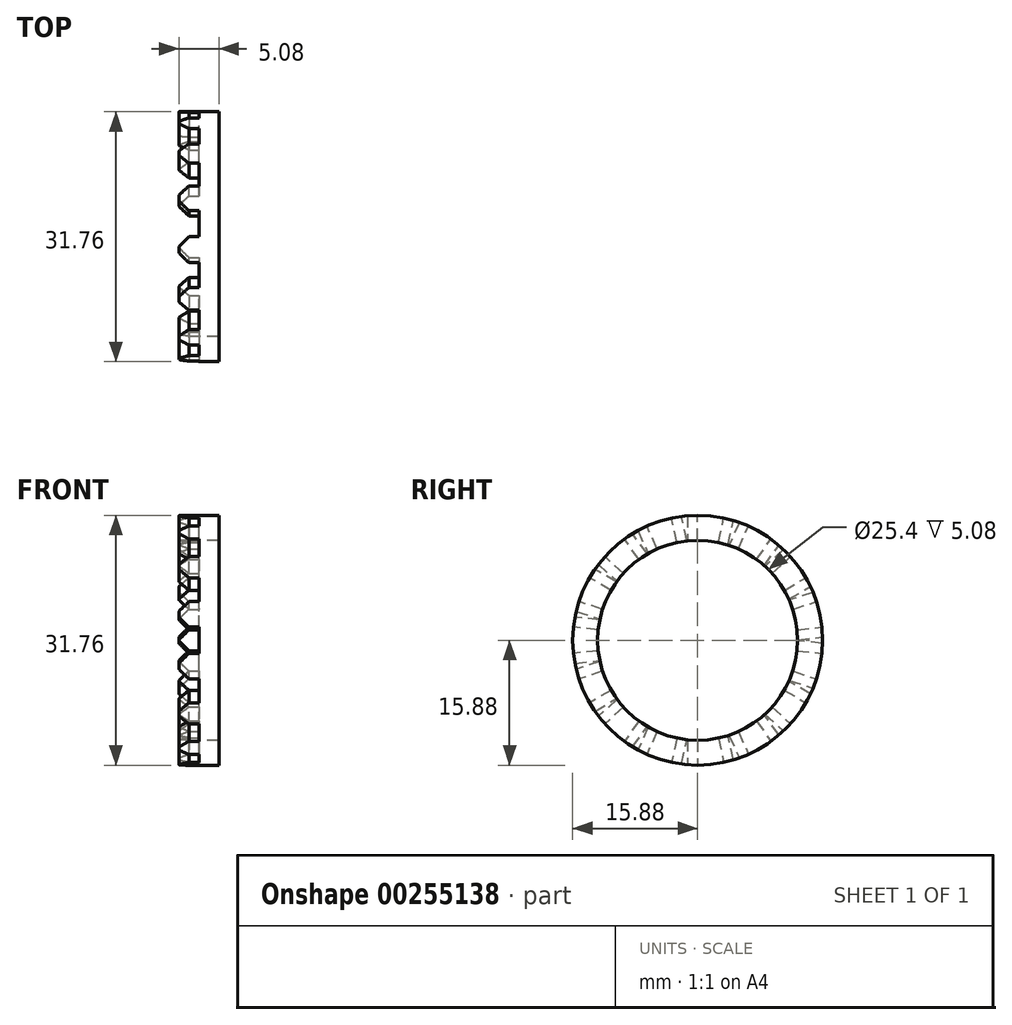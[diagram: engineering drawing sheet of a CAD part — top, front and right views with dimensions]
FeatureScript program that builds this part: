
annotation { "Feature Type Name" : "Feature", "Feature Type Description" : "" }
export const myFeature = defineFeature(function(context is Context, id is Id, definition is map)
    precondition{}
    {
        {
            var Q0;
            Q0=qCreatedBy(makeId("Right.planeOp"),FACE);
            var sketch = newSketch(context, id + "F0", { "sketchPlane" : qUnion([Q0])});
            skCircle(sketch, "E0", {"center": v(0, 0) * mm, "radius": 12.7 * mm});
            skCircle(sketch, "E1", {"center": v(0, 0) * mm, "radius": 15.88 * mm});
            skSolve(sketch);
        }
        {
            var Q0;
            Q0 = qSketchRegion(id + "F0", true);
            extrude(context, id + "F1", {"entities" : qUnion([Q0]), "depth" : 5.08 * mm});
        }
        {
            var Q0;
            Q0=makeQuery(id+"F1.opExtrude","CAP_FACE",FACE,{"disambiguationData":[OSD([sQuery(id+"F0.wireOp",EDGE,"E0"),sQuery(id+"F0.wireOp",EDGE,"E1")])],"isStart":true});
            var sketch = newSketch(context, id + "F2", { "sketchPlane" : qUnion([Q0])});
            skLineSegment(sketch, "E2", {"start": v(0, 12.7) * mm, "end": v(0, 15.88) * mm});
            skLineSegment(sketch, "E3.1.0", {"start": v(-2.64, 12.42) * mm, "end": v(-3.3, 15.53) * mm});
            skLineSegment(sketch, "E3.2.0", {"start": v(-5.17, 11.6) * mm, "end": v(-6.46, 14.5) * mm});
            skLineSegment(sketch, "E3.3.0", {"start": v(-7.46, 10.27) * mm, "end": v(-9.33, 12.84) * mm});
            skLineSegment(sketch, "E3.4.0", {"start": v(-9.44, 8.5) * mm, "end": v(-11.8, 10.62) * mm});
            skLineSegment(sketch, "E3.5.0", {"start": v(-11, 6.35) * mm, "end": v(-13.75, 7.94) * mm});
            skLineSegment(sketch, "E3.6.0", {"start": v(-12.08, 3.92) * mm, "end": v(-15.1, 4.9) * mm});
            skLineSegment(sketch, "E3.7.0", {"start": v(-12.63, 1.33) * mm, "end": v(-15.79, 1.66) * mm});
            skLineSegment(sketch, "E3.8.0", {"start": v(-12.63, -1.33) * mm, "end": v(-15.79, -1.66) * mm});
            skLineSegment(sketch, "E3.9.0", {"start": v(-12.08, -3.92) * mm, "end": v(-15.1, -4.9) * mm});
            skLineSegment(sketch, "E3.10.0", {"start": v(-11, -6.35) * mm, "end": v(-13.75, -7.94) * mm});
            skLineSegment(sketch, "E3.11.0", {"start": v(-9.44, -8.5) * mm, "end": v(-11.8, -10.62) * mm});
            skLineSegment(sketch, "E3.12.0", {"start": v(-7.46, -10.27) * mm, "end": v(-9.33, -12.84) * mm});
            skLineSegment(sketch, "E3.13.0", {"start": v(-5.17, -11.6) * mm, "end": v(-6.46, -14.5) * mm});
            skLineSegment(sketch, "E3.14.0", {"start": v(-2.64, -12.42) * mm, "end": v(-3.3, -15.53) * mm});
            skLineSegment(sketch, "E3.15.0", {"start": v(0, -12.7) * mm, "end": v(0, -15.88) * mm});
            skLineSegment(sketch, "E3.16.0", {"start": v(2.64, -12.42) * mm, "end": v(3.3, -15.53) * mm});
            skLineSegment(sketch, "E3.17.0", {"start": v(5.17, -11.6) * mm, "end": v(6.46, -14.5) * mm});
            skLineSegment(sketch, "E3.18.0", {"start": v(7.46, -10.27) * mm, "end": v(9.33, -12.84) * mm});
            skLineSegment(sketch, "E3.19.0", {"start": v(9.44, -8.5) * mm, "end": v(11.8, -10.62) * mm});
            skLineSegment(sketch, "E3.20.0", {"start": v(11, -6.35) * mm, "end": v(13.75, -7.94) * mm});
            skLineSegment(sketch, "E3.21.0", {"start": v(12.08, -3.92) * mm, "end": v(15.1, -4.9) * mm});
            skLineSegment(sketch, "E3.22.0", {"start": v(12.63, -1.33) * mm, "end": v(15.79, -1.66) * mm});
            skLineSegment(sketch, "E3.23.0", {"start": v(12.63, 1.33) * mm, "end": v(15.79, 1.66) * mm});
            skLineSegment(sketch, "E3.24.0", {"start": v(12.08, 3.92) * mm, "end": v(15.1, 4.9) * mm});
            skLineSegment(sketch, "E3.25.0", {"start": v(11, 6.35) * mm, "end": v(13.75, 7.94) * mm});
            skLineSegment(sketch, "E3.26.0", {"start": v(9.44, 8.5) * mm, "end": v(11.8, 10.62) * mm});
            skLineSegment(sketch, "E3.27.0", {"start": v(7.46, 10.27) * mm, "end": v(9.33, 12.84) * mm});
            skLineSegment(sketch, "E3.28.0", {"start": v(5.17, 11.6) * mm, "end": v(6.46, 14.5) * mm});
            skLineSegment(sketch, "E3.29.0", {"start": v(2.64, 12.42) * mm, "end": v(3.3, 15.53) * mm});
            skPoint(sketch, "E3.center", {"position": v(0, 0) * mm});
            skCircle(sketch, "E4", {"center": v(0, 0) * mm, "radius": 15.88 * mm});
            skCircle(sketch, "E5", {"center": v(0, 0) * mm, "radius": 12.7 * mm});
            skSolve(sketch);
        }
        {
            var Q0;
            {var subQ0=sQuery(id+"F2.wireOp",EDGE,"E3.1.0");Q0=makeQuery(id+"F2.imprint","IMPRINT",FACE,{"disambiguationData":[TD([[makeQuery(id+"F2.imprint","IMPRINT",EDGE,{"derivedFrom":subQ0}),1.0]])]});}
            var Q1;
            {var subQ0=sQuery(id+"F2.wireOp",EDGE,"E2");Q1=makeQuery(id+"F2.imprint","IMPRINT",FACE,{"disambiguationData":[TD([[makeQuery(id+"F2.imprint","IMPRINT",EDGE,{"derivedFrom":subQ0}),-1.0]])]});}
            var Q2;
            {var subQ0=sQuery(id+"F2.wireOp",EDGE,"E3.27.0");Q2=makeQuery(id+"F2.imprint","IMPRINT",FACE,{"disambiguationData":[TD([[makeQuery(id+"F2.imprint","IMPRINT",EDGE,{"derivedFrom":subQ0}),1.0]])]});}
            var Q3;
            {var subQ0=sQuery(id+"F2.wireOp",EDGE,"E3.25.0");Q3=makeQuery(id+"F2.imprint","IMPRINT",FACE,{"disambiguationData":[TD([[makeQuery(id+"F2.imprint","IMPRINT",EDGE,{"derivedFrom":subQ0}),1.0]])]});}
            var Q4;
            {var subQ0=sQuery(id+"F2.wireOp",EDGE,"E3.23.0");Q4=makeQuery(id+"F2.imprint","IMPRINT",FACE,{"disambiguationData":[TD([[makeQuery(id+"F2.imprint","IMPRINT",EDGE,{"derivedFrom":subQ0}),1.0]])]});}
            var Q5;
            {var subQ0=sQuery(id+"F2.wireOp",EDGE,"E3.21.0");Q5=makeQuery(id+"F2.imprint","IMPRINT",FACE,{"disambiguationData":[TD([[makeQuery(id+"F2.imprint","IMPRINT",EDGE,{"derivedFrom":subQ0}),1.0]])]});}
            var Q6;
            {var subQ0=sQuery(id+"F2.wireOp",EDGE,"E3.19.0");Q6=makeQuery(id+"F2.imprint","IMPRINT",FACE,{"disambiguationData":[TD([[makeQuery(id+"F2.imprint","IMPRINT",EDGE,{"derivedFrom":subQ0}),1.0]])]});}
            var Q7;
            {var subQ0=sQuery(id+"F2.wireOp",EDGE,"E3.17.0");Q7=makeQuery(id+"F2.imprint","IMPRINT",FACE,{"disambiguationData":[TD([[makeQuery(id+"F2.imprint","IMPRINT",EDGE,{"derivedFrom":subQ0}),1.0]])]});}
            var Q8;
            {var subQ0=sQuery(id+"F2.wireOp",EDGE,"E3.15.0");Q8=makeQuery(id+"F2.imprint","IMPRINT",FACE,{"disambiguationData":[TD([[makeQuery(id+"F2.imprint","IMPRINT",EDGE,{"derivedFrom":subQ0}),1.0]])]});}
            var Q9;
            {var subQ0=sQuery(id+"F2.wireOp",EDGE,"E3.13.0");Q9=makeQuery(id+"F2.imprint","IMPRINT",FACE,{"disambiguationData":[TD([[makeQuery(id+"F2.imprint","IMPRINT",EDGE,{"derivedFrom":subQ0}),1.0]])]});}
            var Q10;
            {var subQ0=sQuery(id+"F2.wireOp",EDGE,"E3.11.0");Q10=makeQuery(id+"F2.imprint","IMPRINT",FACE,{"disambiguationData":[TD([[makeQuery(id+"F2.imprint","IMPRINT",EDGE,{"derivedFrom":subQ0}),1.0]])]});}
            var Q11;
            {var subQ0=sQuery(id+"F2.wireOp",EDGE,"E3.9.0");Q11=makeQuery(id+"F2.imprint","IMPRINT",FACE,{"disambiguationData":[TD([[makeQuery(id+"F2.imprint","IMPRINT",EDGE,{"derivedFrom":subQ0}),1.0]])]});}
            var Q12;
            {var subQ0=sQuery(id+"F2.wireOp",EDGE,"E3.7.0");Q12=makeQuery(id+"F2.imprint","IMPRINT",FACE,{"disambiguationData":[TD([[makeQuery(id+"F2.imprint","IMPRINT",EDGE,{"derivedFrom":subQ0}),1.0]])]});}
            var Q13;
            {var subQ0=sQuery(id+"F2.wireOp",EDGE,"E3.5.0");Q13=makeQuery(id+"F2.imprint","IMPRINT",FACE,{"disambiguationData":[TD([[makeQuery(id+"F2.imprint","IMPRINT",EDGE,{"derivedFrom":subQ0}),1.0]])]});}
            var Q14;
            {var subQ0=sQuery(id+"F2.wireOp",EDGE,"E3.3.0");Q14=makeQuery(id+"F2.imprint","IMPRINT",FACE,{"disambiguationData":[TD([[makeQuery(id+"F2.imprint","IMPRINT",EDGE,{"derivedFrom":subQ0}),1.0]])]});}
            extrude(context, id + "F3", {"entities" : qUnion([Q0, Q1, Q2, Q3, Q4, Q5, Q6, Q7, Q8, Q9, Q10, Q11, Q12, Q13, Q14]), "operationType" : NewBodyOperationType.ADD, "depth" : 2.54 * mm});
        }
        {
            var Q0;
            Q0=makeQuery(id+"F3.opExtrude","CAP_EDGE",EDGE,{"disambiguationData":[OSD([sQuery(id+"F2.wireOp",EDGE,"E3.5.0")])],"isStart":false});
            var Q1;
            Q1=makeQuery(id+"F3.opExtrude","CAP_EDGE",EDGE,{"disambiguationData":[OSD([sQuery(id+"F2.wireOp",EDGE,"E3.6.0")])],"isStart":false});
            var Q2;
            Q2=makeQuery(id+"F3.opExtrude","CAP_EDGE",EDGE,{"disambiguationData":[OSD([sQuery(id+"F2.wireOp",EDGE,"E3.4.0")])],"isStart":false});
            var Q3;
            Q3=makeQuery(id+"F3.opExtrude","CAP_EDGE",EDGE,{"disambiguationData":[OSD([sQuery(id+"F2.wireOp",EDGE,"E3.3.0")])],"isStart":false});
            var Q4;
            Q4=makeQuery(id+"F3.opExtrude","CAP_EDGE",EDGE,{"disambiguationData":[OSD([sQuery(id+"F2.wireOp",EDGE,"E3.2.0")])],"isStart":false});
            var Q5;
            Q5=makeQuery(id+"F3.opExtrude","CAP_EDGE",EDGE,{"disambiguationData":[OSD([sQuery(id+"F2.wireOp",EDGE,"E3.1.0")])],"isStart":false});
            var Q6;
            Q6=makeQuery(id+"F3.opExtrude","CAP_EDGE",EDGE,{"disambiguationData":[OSD([sQuery(id+"F2.wireOp",EDGE,"E3.29.0")])],"isStart":false});
            var Q7;
            Q7=makeQuery(id+"F3.opExtrude","CAP_EDGE",EDGE,{"disambiguationData":[OSD([sQuery(id+"F2.wireOp",EDGE,"E2")])],"isStart":false});
            var Q8;
            Q8=makeQuery(id+"F3.opExtrude","CAP_EDGE",EDGE,{"disambiguationData":[OSD([sQuery(id+"F2.wireOp",EDGE,"E3.27.0")])],"isStart":false});
            var Q9;
            Q9=makeQuery(id+"F3.opExtrude","CAP_EDGE",EDGE,{"disambiguationData":[OSD([sQuery(id+"F2.wireOp",EDGE,"E3.28.0")])],"isStart":false});
            var Q10;
            Q10=makeQuery(id+"F3.opExtrude","CAP_EDGE",EDGE,{"disambiguationData":[OSD([sQuery(id+"F2.wireOp",EDGE,"E3.26.0")])],"isStart":false});
            var Q11;
            Q11=makeQuery(id+"F3.opExtrude","CAP_EDGE",EDGE,{"disambiguationData":[OSD([sQuery(id+"F2.wireOp",EDGE,"E3.25.0")])],"isStart":false});
            var Q12;
            Q12=makeQuery(id+"F3.opExtrude","CAP_EDGE",EDGE,{"disambiguationData":[OSD([sQuery(id+"F2.wireOp",EDGE,"E3.24.0")])],"isStart":false});
            var Q13;
            Q13=makeQuery(id+"F3.opExtrude","CAP_EDGE",EDGE,{"disambiguationData":[OSD([sQuery(id+"F2.wireOp",EDGE,"E3.23.0")])],"isStart":false});
            var Q14;
            Q14=makeQuery(id+"F3.opExtrude","CAP_EDGE",EDGE,{"disambiguationData":[OSD([sQuery(id+"F2.wireOp",EDGE,"E3.22.0")])],"isStart":false});
            var Q15;
            Q15=makeQuery(id+"F3.opExtrude","CAP_EDGE",EDGE,{"disambiguationData":[OSD([sQuery(id+"F2.wireOp",EDGE,"E3.21.0")])],"isStart":false});
            var Q16;
            Q16=makeQuery(id+"F3.opExtrude","CAP_EDGE",EDGE,{"disambiguationData":[OSD([sQuery(id+"F2.wireOp",EDGE,"E3.20.0")])],"isStart":false});
            var Q17;
            Q17=makeQuery(id+"F3.opExtrude","CAP_EDGE",EDGE,{"disambiguationData":[OSD([sQuery(id+"F2.wireOp",EDGE,"E3.19.0")])],"isStart":false});
            var Q18;
            Q18=makeQuery(id+"F3.opExtrude","CAP_EDGE",EDGE,{"disambiguationData":[OSD([sQuery(id+"F2.wireOp",EDGE,"E3.18.0")])],"isStart":false});
            var Q19;
            Q19=makeQuery(id+"F3.opExtrude","CAP_EDGE",EDGE,{"disambiguationData":[OSD([sQuery(id+"F2.wireOp",EDGE,"E3.17.0")])],"isStart":false});
            var Q20;
            Q20=makeQuery(id+"F3.opExtrude","CAP_EDGE",EDGE,{"disambiguationData":[OSD([sQuery(id+"F2.wireOp",EDGE,"E3.16.0")])],"isStart":false});
            var Q21;
            Q21=makeQuery(id+"F3.opExtrude","CAP_EDGE",EDGE,{"disambiguationData":[OSD([sQuery(id+"F2.wireOp",EDGE,"E3.15.0")])],"isStart":false});
            var Q22;
            Q22=makeQuery(id+"F3.opExtrude","CAP_EDGE",EDGE,{"disambiguationData":[OSD([sQuery(id+"F2.wireOp",EDGE,"E3.14.0")])],"isStart":false});
            var Q23;
            Q23=makeQuery(id+"F3.opExtrude","CAP_EDGE",EDGE,{"disambiguationData":[OSD([sQuery(id+"F2.wireOp",EDGE,"E3.13.0")])],"isStart":false});
            var Q24;
            Q24=makeQuery(id+"F3.opExtrude","CAP_EDGE",EDGE,{"disambiguationData":[OSD([sQuery(id+"F2.wireOp",EDGE,"E3.12.0")])],"isStart":false});
            var Q25;
            Q25=makeQuery(id+"F3.opExtrude","CAP_EDGE",EDGE,{"disambiguationData":[OSD([sQuery(id+"F2.wireOp",EDGE,"E3.11.0")])],"isStart":false});
            var Q26;
            Q26=makeQuery(id+"F3.opExtrude","CAP_EDGE",EDGE,{"disambiguationData":[OSD([sQuery(id+"F2.wireOp",EDGE,"E3.10.0")])],"isStart":false});
            var Q27;
            Q27=makeQuery(id+"F3.opExtrude","CAP_EDGE",EDGE,{"disambiguationData":[OSD([sQuery(id+"F2.wireOp",EDGE,"E3.9.0")])],"isStart":false});
            var Q28;
            Q28=makeQuery(id+"F3.opExtrude","CAP_EDGE",EDGE,{"disambiguationData":[OSD([sQuery(id+"F2.wireOp",EDGE,"E3.8.0")])],"isStart":false});
            var Q29;
            Q29=makeQuery(id+"F3.opExtrude","CAP_EDGE",EDGE,{"disambiguationData":[OSD([sQuery(id+"F2.wireOp",EDGE,"E3.7.0")])],"isStart":false});
            chamfer(context, id + "F4", {"entities" : qUnion([Q0, Q1, Q2, Q3, Q4, Q5, Q6, Q7, Q8, Q9, Q10, Q11, Q12, Q13, Q14, Q15, Q16, Q17, Q18, Q19, Q20, Q21, Q22, Q23, Q24, Q25, Q26, Q27, Q28, Q29]), "width" : 1.27 * mm, "tangentPropagation" : true});
        }
        {
            var Q0;
            Q0=makeQuery(id+"F1.opExtrude","CAP_FACE",FACE,{"disambiguationData":[OSD([sQuery(id+"F0.wireOp",EDGE,"E0"),sQuery(id+"F0.wireOp",EDGE,"E1")])],"isStart":false});
            extrude(context, id + "F5", {"entities" : qUnion([Q0]), "operationType" : NewBodyOperationType.REMOVE, "oppositeDirection" : true, "depth" : 2.54 * mm});
        }
    });
